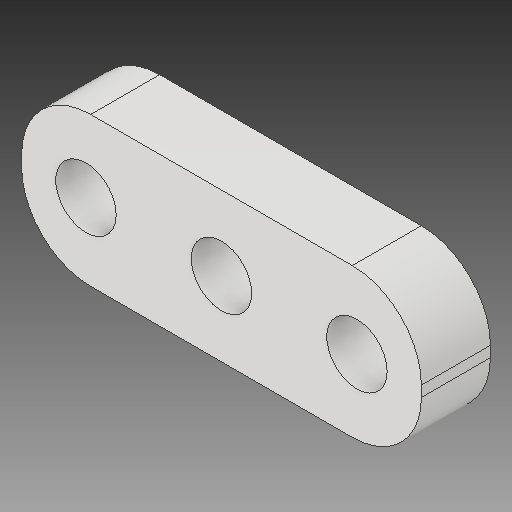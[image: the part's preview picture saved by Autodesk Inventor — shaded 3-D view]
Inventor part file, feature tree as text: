
AUTODESK INVENTOR PART (.ipt)
format: ipt  version: 2018 (Build 220112000, 112)  size: 113,664 bytes
history: native  units: in
note: dims shown in document units (in); Inventor stores cm internally (conversion verified against a paired STEP export)
features: fillet x1
ambient origin geometry x8: Origin, YZ Plane, XZ Plane, XY Plane, X Axis, Y Axis, Z Axis, Center Point
bodies: Solid1 (feature_tree)
feature tree (1):
  fillet  "Fillet1"  [1 undecoded]
note: 1 required parameter value undecoded (feature->parameter linkage not recoverable at this tier; creation-order binding heuristic only, values carry confidence <= 0.55)
